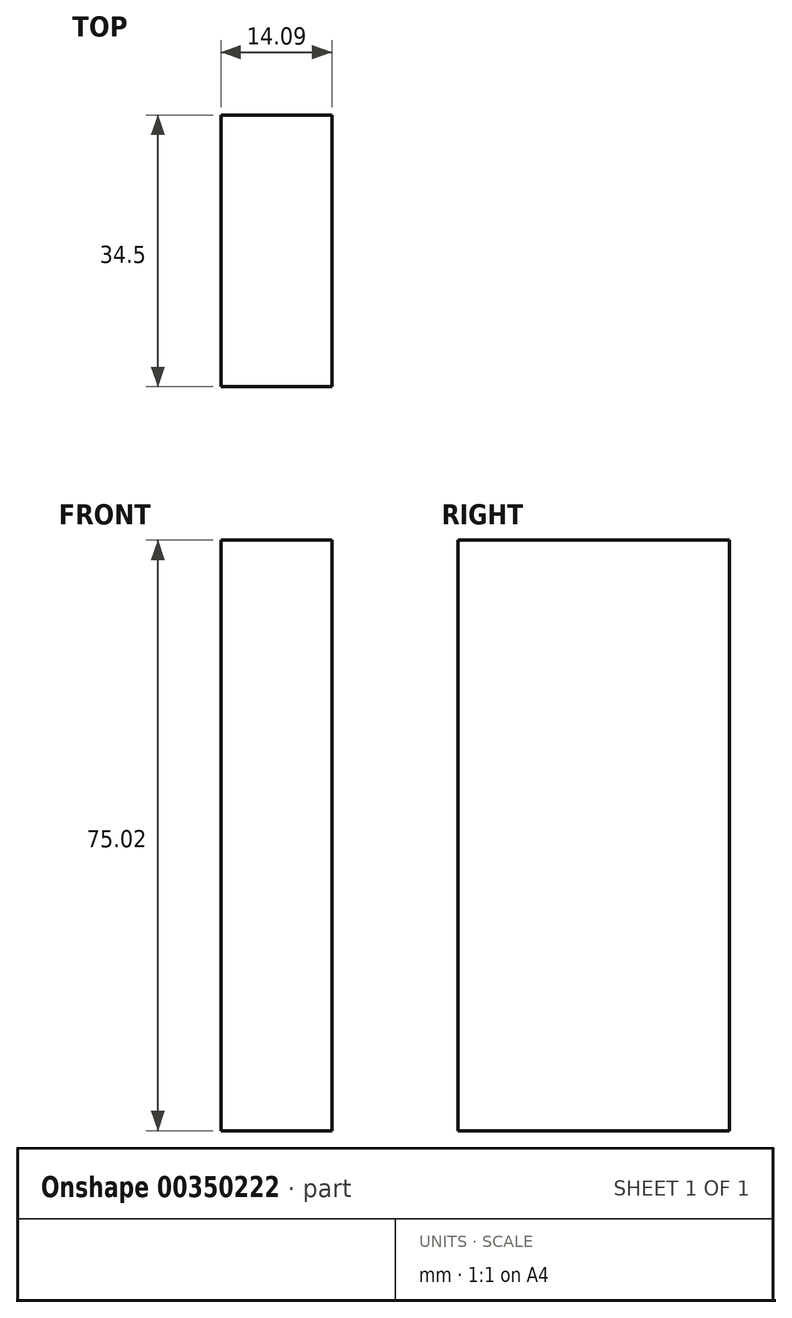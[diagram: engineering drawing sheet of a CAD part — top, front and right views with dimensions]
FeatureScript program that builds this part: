
annotation { "Feature Type Name" : "Feature", "Feature Type Description" : "" }
export const myFeature = defineFeature(function(context is Context, id is Id, definition is map)
    precondition{}
    {
        {
            var Q0;
            Q0=qCreatedBy(makeId("Front.planeOp"),FACE);
            var sketch = newSketch(context, id + "F0", { "sketchPlane" : qUnion([Q0])});
            skLineSegment(sketch, "E0.bottom", {"start": v(0, 75.02) * mm, "end": v(14.1, 75.02) * mm});
            skLineSegment(sketch, "E0.top", {"start": v(0, 0) * mm, "end": v(14.1, 0) * mm});
            skLineSegment(sketch, "E0.left", {"start": v(0, 75.02) * mm, "end": v(0, 0) * mm});
            skLineSegment(sketch, "E0.right", {"start": v(14.1, 75.02) * mm, "end": v(14.1, 0) * mm});
            skSolve(sketch);
        }
        {
            var Q0;
            Q0=makeQuery(id+"F0.imprint","IMPRINT",FACE,{"disambiguationData":[TD([[makeQuery(id+"F0.imprint","IMPRINT",EDGE,{"derivedFrom":sQuery(id+"F0.wireOp",EDGE,"E0.bottom")}),-1.0]])]});
            extrude(context, id + "F1", {"entities" : qUnion([Q0]), "depth" : 34.5 * mm});
        }
    });
